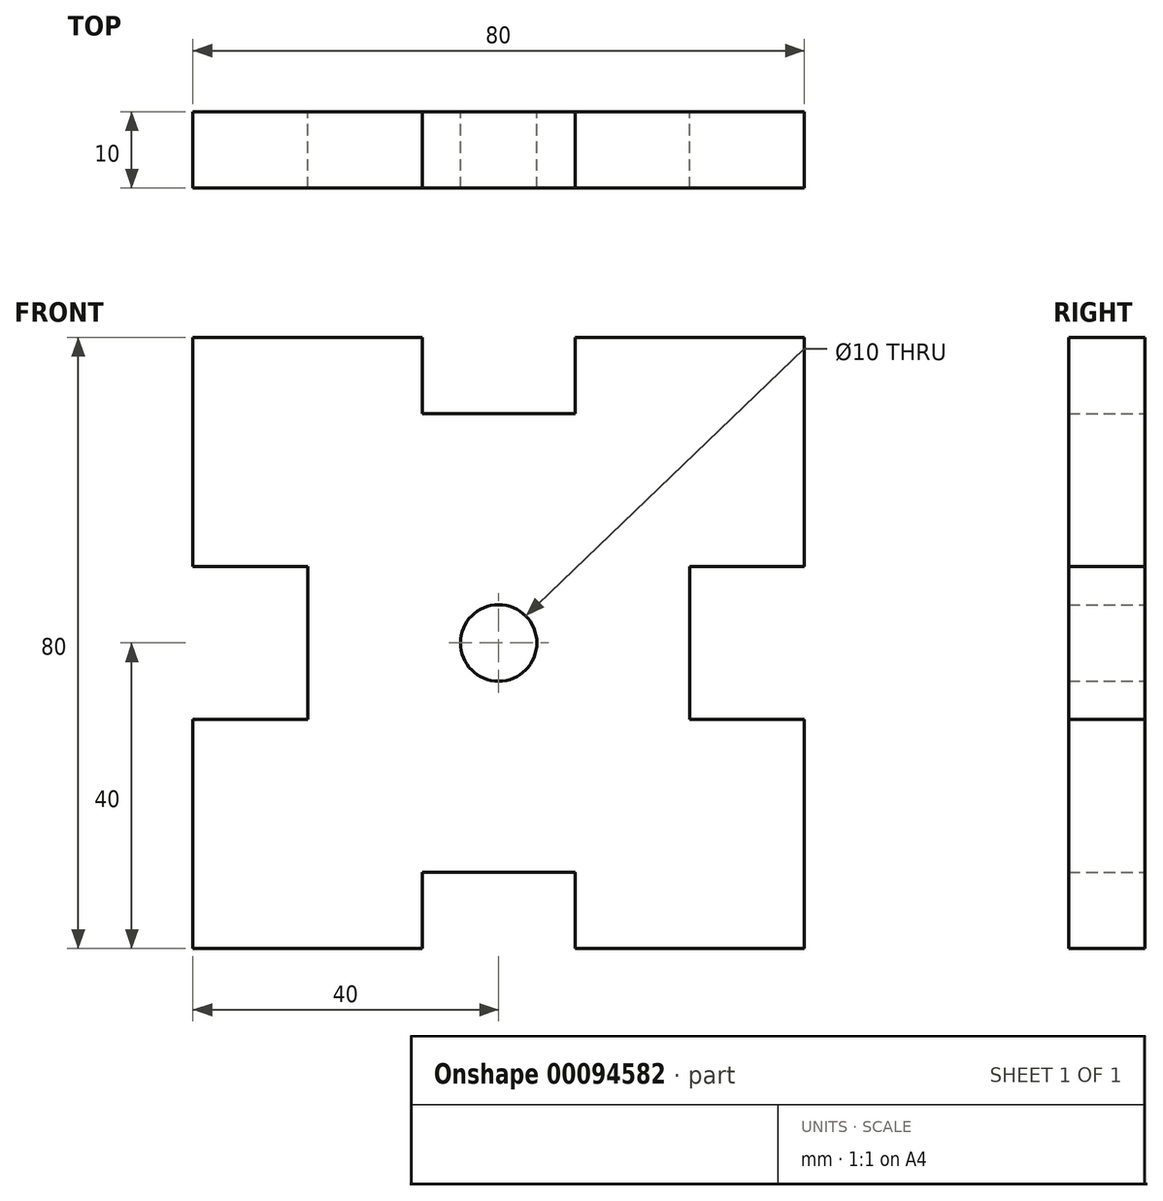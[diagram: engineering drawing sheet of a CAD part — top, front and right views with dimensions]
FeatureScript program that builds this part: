
annotation { "Feature Type Name" : "Feature", "Feature Type Description" : "" }
export const myFeature = defineFeature(function(context is Context, id is Id, definition is map)
    precondition{}
    {
        {
            var Q0;
            Q0=qCreatedBy(makeId("Front.planeOp"),FACE);
            var sketch = newSketch(context, id + "F0", { "sketchPlane" : qUnion([Q0])});
            skLineSegment(sketch, "E0", {"start": v(0, -51.02) * mm, "end": v(0, 55.23) * mm, "construction": true});
            skLineSegment(sketch, "E1", {"start": v(-44.97, 0) * mm, "end": v(50.44, 0) * mm, "construction": true});
            skLineSegment(sketch, "E2", {"start": v(0, 30) * mm, "end": v(-10, 30) * mm});
            skLineSegment(sketch, "E3", {"start": v(-10, 30) * mm, "end": v(-10, 40) * mm});
            skLineSegment(sketch, "E4", {"start": v(-10, 40) * mm, "end": v(-40, 40) * mm});
            skLineSegment(sketch, "E5", {"start": v(-40, 40) * mm, "end": v(-40, 10) * mm});
            skLineSegment(sketch, "E6", {"start": v(-40, 10) * mm, "end": v(-25, 10) * mm});
            skLineSegment(sketch, "E7", {"start": v(-25, 10) * mm, "end": v(-25, 0) * mm});
            skLineSegment(sketch, "E8.MirrorCS", {"start": v(-25, -10) * mm, "end": v(-25, 0) * mm});
            skLineSegment(sketch, "E9.MirrorCS", {"start": v(-40, -10) * mm, "end": v(-25, -10) * mm});
            skLineSegment(sketch, "E10.MirrorCS", {"start": v(-40, -40) * mm, "end": v(-40, -10) * mm});
            skLineSegment(sketch, "E11.MirrorCS", {"start": v(-10, -40) * mm, "end": v(-40, -40) * mm});
            skLineSegment(sketch, "E12.MirrorCS", {"start": v(-10, -30) * mm, "end": v(-10, -40) * mm});
            skLineSegment(sketch, "E13.MirrorCS", {"start": v(0, -30) * mm, "end": v(-10, -30) * mm});
            skLineSegment(sketch, "E14.MirrorCS", {"start": v(0, 30) * mm, "end": v(10, 30) * mm});
            skLineSegment(sketch, "E15.MirrorCS", {"start": v(10, 30) * mm, "end": v(10, 40) * mm});
            skLineSegment(sketch, "E16.MirrorCS", {"start": v(10, 40) * mm, "end": v(40, 40) * mm});
            skLineSegment(sketch, "E17.MirrorCS", {"start": v(40, 40) * mm, "end": v(40, 10) * mm});
            skLineSegment(sketch, "E18.MirrorCS", {"start": v(40, 10) * mm, "end": v(25, 10) * mm});
            skLineSegment(sketch, "E19.MirrorCS", {"start": v(25, 10) * mm, "end": v(25, 0) * mm});
            skLineSegment(sketch, "E20.MirrorCS", {"start": v(25, -10) * mm, "end": v(25, 0) * mm});
            skLineSegment(sketch, "E21.MirrorCS", {"start": v(0, -30) * mm, "end": v(10, -30) * mm});
            skLineSegment(sketch, "E22.MirrorCS", {"start": v(10, -30) * mm, "end": v(10, -40) * mm});
            skLineSegment(sketch, "E23.MirrorCS", {"start": v(10, -40) * mm, "end": v(40, -40) * mm});
            skLineSegment(sketch, "E24.MirrorCS", {"start": v(40, -40) * mm, "end": v(40, -10) * mm});
            skLineSegment(sketch, "E25.MirrorCS", {"start": v(40, -10) * mm, "end": v(25, -10) * mm});
            skCircle(sketch, "E26", {"center": v(0, 0) * mm, "radius": 5 * mm});
            skSolve(sketch);
        }
        {
            var Q0;
            Q0=makeQuery(id+"F0.imprint","IMPRINT",FACE,{"disambiguationData":[TD([[makeQuery(id+"F0.imprint","IMPRINT",EDGE,{"derivedFrom":sQuery(id+"F0.wireOp",EDGE,"E2")}),1.0]])]});
            extrude(context, id + "F1", {"entities" : qUnion([Q0]), "depth" : 10 * mm});
        }
    });
